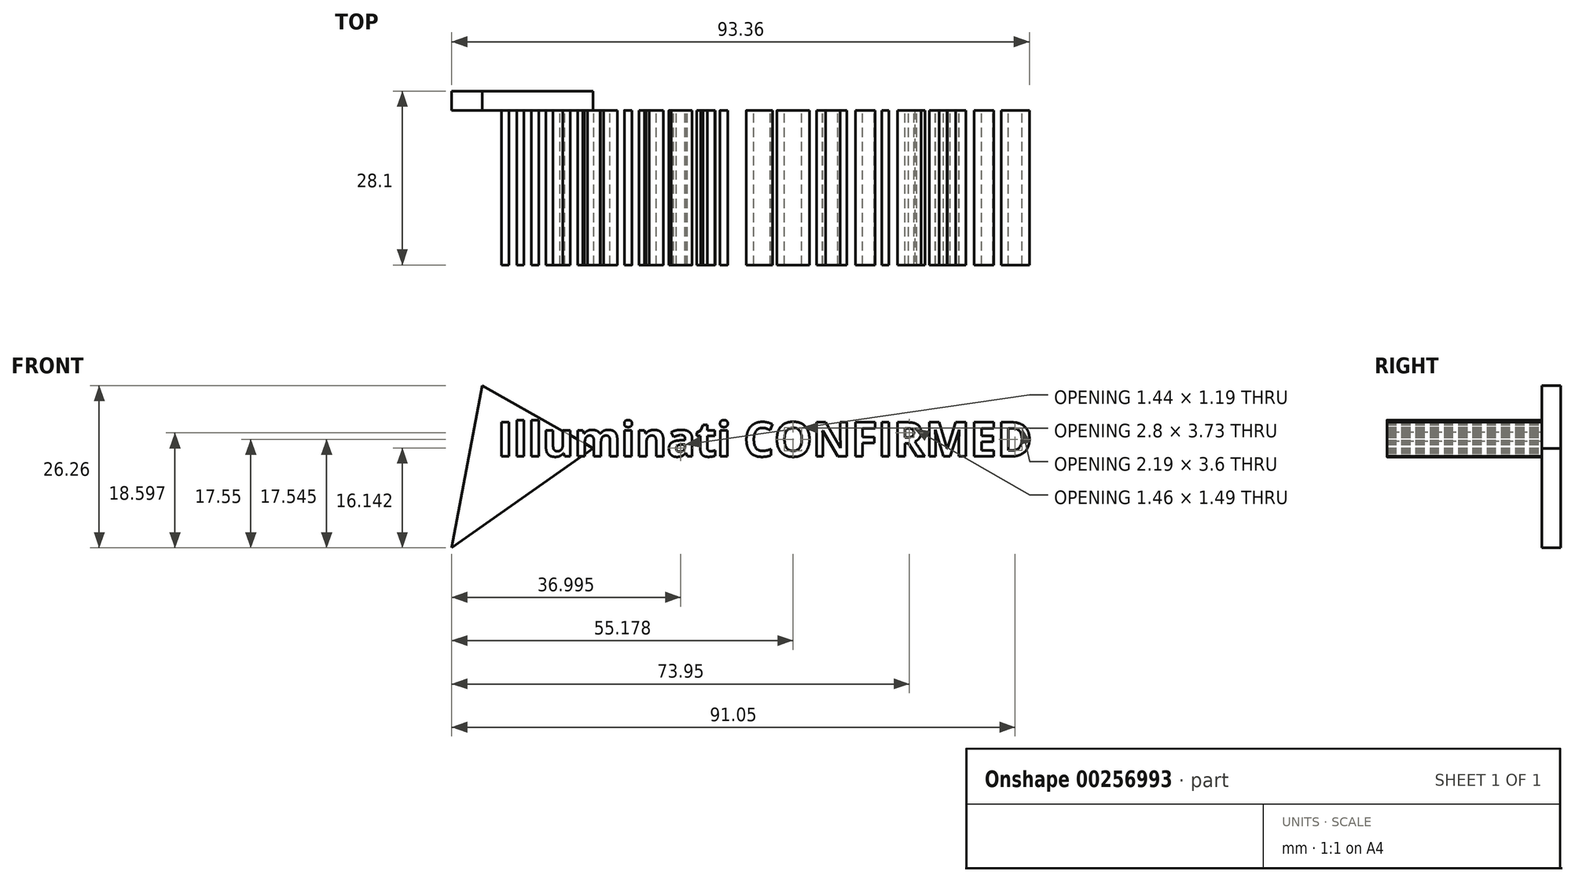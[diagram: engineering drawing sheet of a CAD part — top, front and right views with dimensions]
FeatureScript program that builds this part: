
annotation { "Feature Type Name" : "Feature", "Feature Type Description" : "" }
export const myFeature = defineFeature(function(context is Context, id is Id, definition is map)
    precondition{}
    {
        {
            var Q0;
            Q0=qCreatedBy(makeId("Front.planeOp"),FACE);
            var sketch = newSketch(context, id + "F0", { "sketchPlane" : qUnion([Q0])});
            skLineSegment(sketch, "E0", {"start": v(0, 0) * mm, "end": v(4.92, 26.26) * mm});
            skLineSegment(sketch, "E1", {"start": v(4.92, 26.26) * mm, "end": v(22.86, 16.1) * mm});
            skLineSegment(sketch, "E2", {"start": v(0, 0) * mm, "end": v(22.86, 16.1) * mm});
            skSolve(sketch);
        }
        {
            var Q0;
            Q0=makeQuery(id+"F0.imprint","IMPRINT",FACE,{"disambiguationData":[TD([[makeQuery(id+"F0.imprint","IMPRINT",EDGE,{"derivedFrom":sQuery(id+"F0.wireOp",EDGE,"E0")}),-1.0]])]});
            extrude(context, id + "F1", {"entities" : qUnion([Q0]), "depth" : 3.1 * mm});
        }
        {
            var Q0;
            Q0=makeQuery(id+"F1.opExtrude","CAP_FACE",FACE,{"disambiguationData":[OSD([sQuery(id+"F0.wireOp",EDGE,"E0"),sQuery(id+"F0.wireOp",EDGE,"E1"),sQuery(id+"F0.wireOp",EDGE,"E2")])],"isStart":false});
            var sketch = newSketch(context, id + "F2", { "sketchPlane" : qUnion([Q0])});
            skLineSegment(sketch, "E3", {"start": v(12.26, 9.98) * mm, "end": v(10.58, 9.59) * mm});
            skLineSegment(sketch, "E4", {"start": v(10.58, 9.59) * mm, "end": v(9.54, 9.89) * mm});
            skLineSegment(sketch, "E5", {"start": v(9.41, 9.94) * mm, "end": v(8, 10.52) * mm});
            skLineSegment(sketch, "E6", {"start": v(8, 10.52) * mm, "end": v(6.26, 11.88) * mm});
            skLineSegment(sketch, "E7", {"start": v(9.41, 9.94) * mm, "end": v(9.54, 9.89) * mm});
            skLineSegment(sketch, "E8", {"start": v(6.26, 11.88) * mm, "end": v(4.95, 13.25) * mm});
            skLineSegment(sketch, "E9", {"start": v(4.95, 13.25) * mm, "end": v(4.15, 14.26) * mm});
            skLineSegment(sketch, "E10", {"start": v(4.15, 14.26) * mm, "end": v(3.6, 15.54) * mm});
            skLineSegment(sketch, "E11", {"start": v(3.6, 15.54) * mm, "end": v(4.48, 16.32) * mm});
            skLineSegment(sketch, "E12", {"start": v(4.55, 16.38) * mm, "end": v(5.92, 16.32) * mm});
            skLineSegment(sketch, "E13", {"start": v(5.95, 16.32) * mm, "end": v(7.67, 15.8) * mm});
            skLineSegment(sketch, "E14", {"start": v(7.76, 15.82) * mm, "end": v(9.85, 14.8) * mm});
            skLineSegment(sketch, "E15", {"start": v(9.91, 14.8) * mm, "end": v(11.7, 13.56) * mm});
            skLineSegment(sketch, "E16", {"start": v(11.79, 13.47) * mm, "end": v(12.53, 11.78) * mm});
            skLineSegment(sketch, "E17", {"start": v(12.53, 11.78) * mm, "end": v(12.77, 10.36) * mm});
            skLineSegment(sketch, "E18", {"start": v(12.78, 10.32) * mm, "end": v(12.26, 9.98) * mm});
            skLineSegment(sketch, "E19", {"start": v(11.7, 13.56) * mm, "end": v(11.79, 13.47) * mm});
            skCircle(sketch, "E20", {"center": v(8.53, 13.16) * mm, "radius": 2.04 * mm});
            skSolve(sketch);
        }
        {
            var Q0;
            Q0=makeQuery(id+"F2.imprint","IMPRINT",FACE,{"disambiguationData":[TD([[makeQuery(id+"F2.imprint","IMPRINT",EDGE,{"derivedFrom":sQuery(id+"F2.wireOp",EDGE,"E20")}),-1.0]])]});
            var sketch = newSketch(context, id + "F3", { "sketchPlane" : qUnion([Q0])});
            skText(sketch, "E21", { "text": "Illuminati CONFIRMED", "fontName": "OpenSans-Bold.ttf"});
            const initialGuessF3  = {"E21": [0.00736, 0.01478, 1, 0, 0.00557]};
            skSetInitialGuess(sketch, initialGuessF3);
            skSolve(sketch);
        }
        {
            var Q0;
            Q0 = qSketchRegion(id + "F3", true);
            extrude(context, id + "F4", {"entities" : qUnion([Q0]), "operationType" : NewBodyOperationType.ADD, "depth" : 25 * mm});
        }
    });
